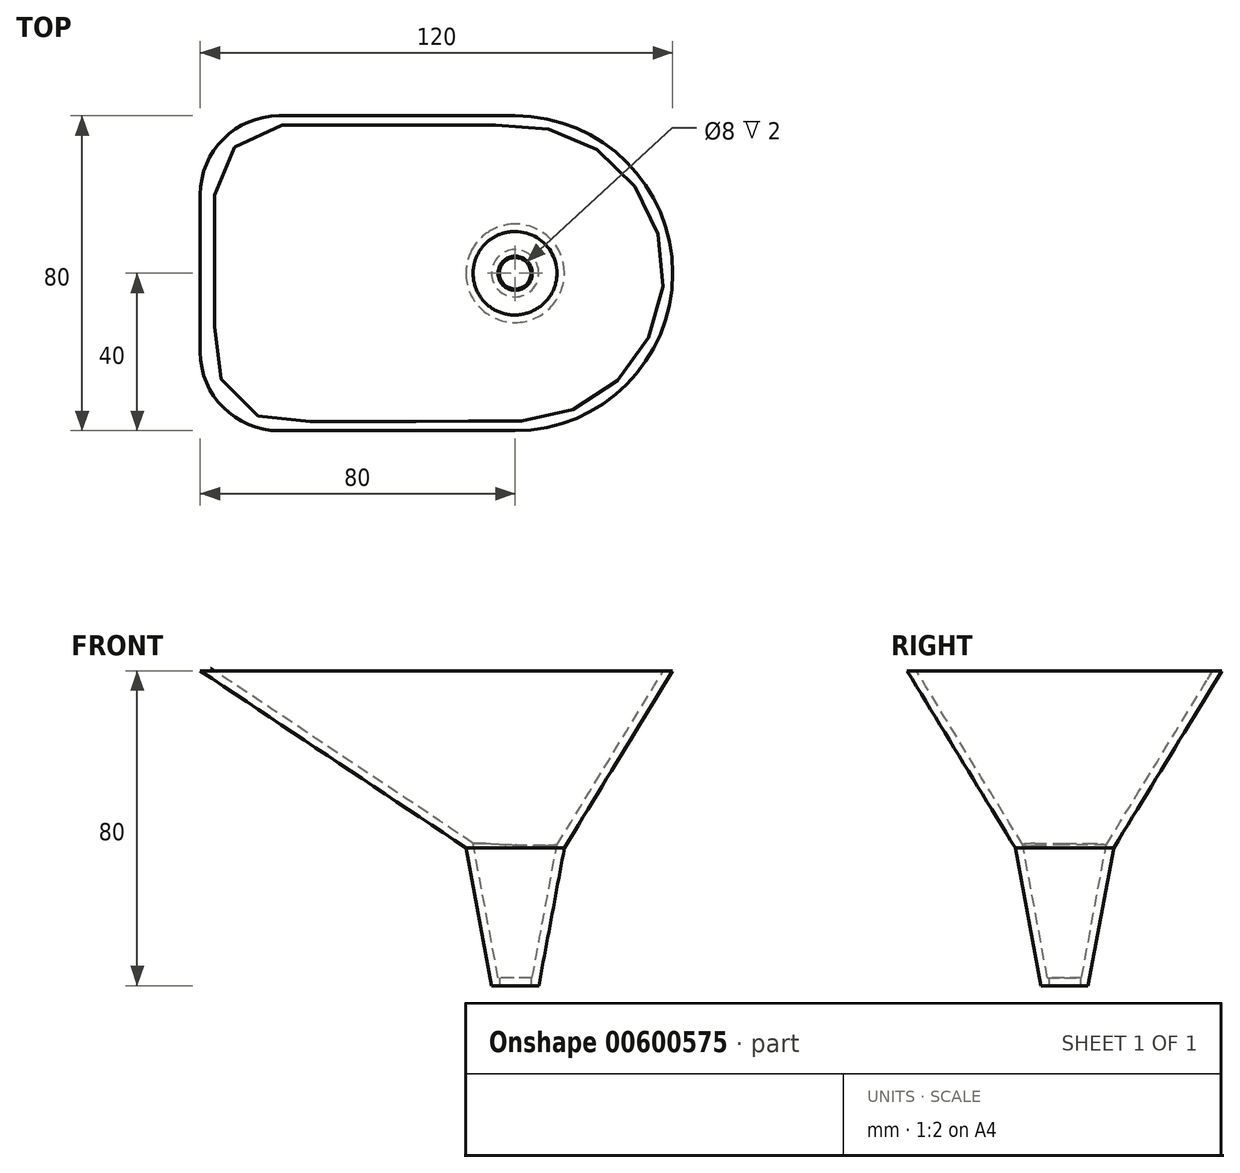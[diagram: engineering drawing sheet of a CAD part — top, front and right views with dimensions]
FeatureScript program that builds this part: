
annotation { "Feature Type Name" : "Feature", "Feature Type Description" : "" }
export const myFeature = defineFeature(function(context is Context, id is Id, definition is map)
    precondition{}
    {
        {
            var Q0;
            Q0=qCreatedBy(makeId("Top.planeOp"),FACE);
            var sketch = newSketch(context, id + "F0", { "sketchPlane" : qUnion([Q0])});
            skCircle(sketch, "E0", {"center": v(0, 0) * mm, "radius": 6 * mm});
            skSolve(sketch);
        }
        {
            var Q0;
            Q0=qCreatedBy(makeId("Top.planeOp"),FACE);
            cPlane(context, id + "F1", {"entities" : qUnion([Q0]), "cplaneType" : CPlaneType.OFFSET, "offset" : 35 * mm, "width" : 150 * mm, "height" : 150 * mm});
        }
        {
            var Q0;
            Q0=qCreatedBy(id+"F1.planeOp",FACE);
            cPlane(context, id + "F2", {"entities" : qUnion([Q0]), "cplaneType" : CPlaneType.OFFSET, "offset" : 45 * mm, "width" : 150 * mm, "height" : 150 * mm});
        }
        {
            var Q0;
            Q0=qCreatedBy(id+"F1.planeOp",FACE);
            var sketch = newSketch(context, id + "F3", { "sketchPlane" : qUnion([Q0])});
            skCircle(sketch, "E1", {"center": v(0, 0) * mm, "radius": 12.5 * mm});
            skSolve(sketch);
        }
        {
            var Q0;
            Q0=qCreatedBy(id+"F2.planeOp",FACE);
            var sketch = newSketch(context, id + "F4", { "sketchPlane" : qUnion([Q0])});
            skLineSegment(sketch, "E2.bottom", {"start": v(-60, 40) * mm, "end": v(0, 40) * mm});
            skLineSegment(sketch, "E2.top", {"start": v(-60, -40) * mm, "end": v(0, -40) * mm});
            skLineSegment(sketch, "E2.left", {"start": v(-80, 20) * mm, "end": v(-80, -20) * mm});
            skLineSegment(sketch, "E2.right", {"start": v(40, 0) * mm, "end": v(40, 0) * mm});
            skPoint(sketch, "E3.visualSharp", {"position": v(40, 40) * mm});
            skArc(sketch, "E3.filletArc", {"start": v(40, 0) * mm, "mid": v(28.28, 28.28) * mm, "end": v(0, 40) * mm});
            skPoint(sketch, "E4.visualSharp", {"position": v(40, -40) * mm});
            skArc(sketch, "E4.filletArc", {"start": v(0, -40) * mm, "mid": v(28.28, -28.28) * mm, "end": v(40, 0) * mm});
            skPoint(sketch, "E5.visualSharp", {"position": v(-80, 40) * mm});
            skArc(sketch, "E5.filletArc", {"start": v(-60, 40) * mm, "mid": v(-74.14, 34.14) * mm, "end": v(-80, 20) * mm});
            skPoint(sketch, "E6.visualSharp", {"position": v(-80, -40) * mm});
            skArc(sketch, "E6.filletArc", {"start": v(-80, -20) * mm, "mid": v(-74.14, -34.14) * mm, "end": v(-60, -40) * mm});
            skSolve(sketch);
        }
        {
            var Q0;
            Q0=qCreatedBy(makeId("Front.planeOp"),FACE);
            var sketch = newSketch(context, id + "F5", { "sketchPlane" : qUnion([Q0])});
            skLineSegment(sketch, "E7", {"start": v(6, 0) * mm, "end": v(12.5, 35) * mm});
            skLineSegment(sketch, "E8", {"start": v(12.5, 35) * mm, "end": v(40, 80) * mm});
            skSolve(sketch);
        }
        {
            var Q0;
            Q0=makeQuery(id+"F3.imprint","IMPRINT",FACE,{"disambiguationData":[TD([[makeQuery(id+"F3.imprint","IMPRINT",EDGE,{"derivedFrom":sQuery(id+"F3.wireOp",EDGE,"E1")}),1.0]])]});
            var Q1;
            Q1=makeQuery(id+"F0.imprint","IMPRINT",FACE,{"disambiguationData":[TD([[makeQuery(id+"F0.imprint","IMPRINT",EDGE,{"derivedFrom":sQuery(id+"F0.wireOp",EDGE,"E0")}),1.0]])]});
            var Q2;
            Q2=sQuery(id+"F0.wireOp",EDGE,"E0");
            var Q3;
            Q3=sQuery(id+"F3.wireOp",EDGE,"E1");
            loft(context, id + "F6", {"sheetProfilesArray" : [{ "sheetProfileEntities" : qUnion([Q0]) }, { "sheetProfileEntities" : qUnion([Q1]) }], "wireProfilesArray" : [{ "wireProfileEntities" : qUnion([Q2]) }, { "wireProfileEntities" : qUnion([Q3]) }]});
        }
        {
            var Q0;
            Q0=qCreatedBy(makeId("Right.planeOp"),FACE);
            var sketch = newSketch(context, id + "F7", { "sketchPlane" : qUnion([Q0])});
            skLineSegment(sketch, "E9", {"start": v(-12.5, 35) * mm, "end": v(-40, 80) * mm});
            skLineSegment(sketch, "E10", {"start": v(40, 80) * mm, "end": v(12.5, 35) * mm});
            skSolve(sketch);
        }
        {
            var Q0;
            Q0=qCreatedBy(makeId("Front.planeOp"),FACE);
            var sketch = newSketch(context, id + "F8", { "sketchPlane" : qUnion([Q0])});
            skLineSegment(sketch, "E11", {"start": v(-80, 80) * mm, "end": v(-12.5, 35) * mm});
            skSolve(sketch);
        }
        {
            var Q1;
            Q1=makeQuery(id+"F6.opLoft","CAP_FACE",FACE,{"disambiguationData":[OSD([makeQuery(id+"F3.imprint","IMPRINT",FACE,{"disambiguationData":[TD([[makeQuery(id+"F3.imprint","IMPRINT",EDGE,{"derivedFrom":sQuery(id+"F3.wireOp",EDGE,"E1")}),1.0]])]})])],"isStart":true});
            var Q2;
            Q2=makeQuery(id+"F4.imprint","IMPRINT",FACE,{"disambiguationData":[TD([[makeQuery(id+"F4.imprint","IMPRINT",EDGE,{"derivedFrom":sQuery(id+"F4.wireOp",EDGE,"E2.bottom")}),-1.0]])]});
            var Q3;
            Q3=sQuery(id+"F7.wireOp",EDGE,"E10");
            var Q4;
            Q4=sQuery(id+"F8.wireOp",EDGE,"E11");
            var Q5;
            Q5=sQuery(id+"F5.wireOp",EDGE,"E8");
            loft(context, id + "F9", {"operationType" : NewBodyOperationType.ADD, "addGuides" : true, "sheetProfilesArray" : [{ "sheetProfileEntities" : qUnion([Q1]) }, { "sheetProfileEntities" : qUnion([Q2]) }], "guidesArray" : [{ "guideEntities" : qUnion([Q3]), "guideDerivativeType" : LoftGuideDerivativeType.DEFAULT, "guideDerivativeMagnitude" : 1 }, { "guideEntities" : qUnion([Q4]), "guideDerivativeType" : LoftGuideDerivativeType.DEFAULT, "guideDerivativeMagnitude" : 1 }, { "guideEntities" : qUnion([Q5]), "guideDerivativeType" : LoftGuideDerivativeType.DEFAULT, "guideDerivativeMagnitude" : 1 }]});
        }
        {
            var Q0;
            Q0=makeQuery(id+"F9.opLoft","CAP_FACE",FACE,{"disambiguationData":[OSD([makeQuery(id+"F4.imprint","IMPRINT",FACE,{"disambiguationData":[TD([[makeQuery(id+"F4.imprint","IMPRINT",EDGE,{"derivedFrom":sQuery(id+"F4.wireOp",EDGE,"E2.bottom")}),-1.0]])]})])],"isStart":true});
            shell(context, id + "F10", {"entities" : qUnion([Q0]), "thickness" : 2 * mm});
        }
        {
            var Q0;
            Q0=makeQuery(id+"F6.opLoft","CAP_FACE",FACE,{"disambiguationData":[OSD([makeQuery(id+"F0.imprint","IMPRINT",FACE,{"disambiguationData":[TD([[makeQuery(id+"F0.imprint","IMPRINT",EDGE,{"derivedFrom":sQuery(id+"F0.wireOp",EDGE,"E0")}),1.0]])]})])],"isStart":true});
            var sketch = newSketch(context, id + "F11", { "sketchPlane" : qUnion([Q0])});
            skCircle(sketch, "E12", {"center": v(0, 0) * mm, "radius": 4 * mm});
            skSolve(sketch);
        }
        {
            var Q0;
            Q0 = qSketchRegion(id + "F11", true);
            extrude(context, id + "F12", {"entities" : qUnion([Q0]), "operationType" : NewBodyOperationType.REMOVE, "endBound" : BoundingType.THROUGH_ALL, "oppositeDirection" : true, "depth" : 25 * mm, "offsetDistance" : 25 * mm});
        }
    });
